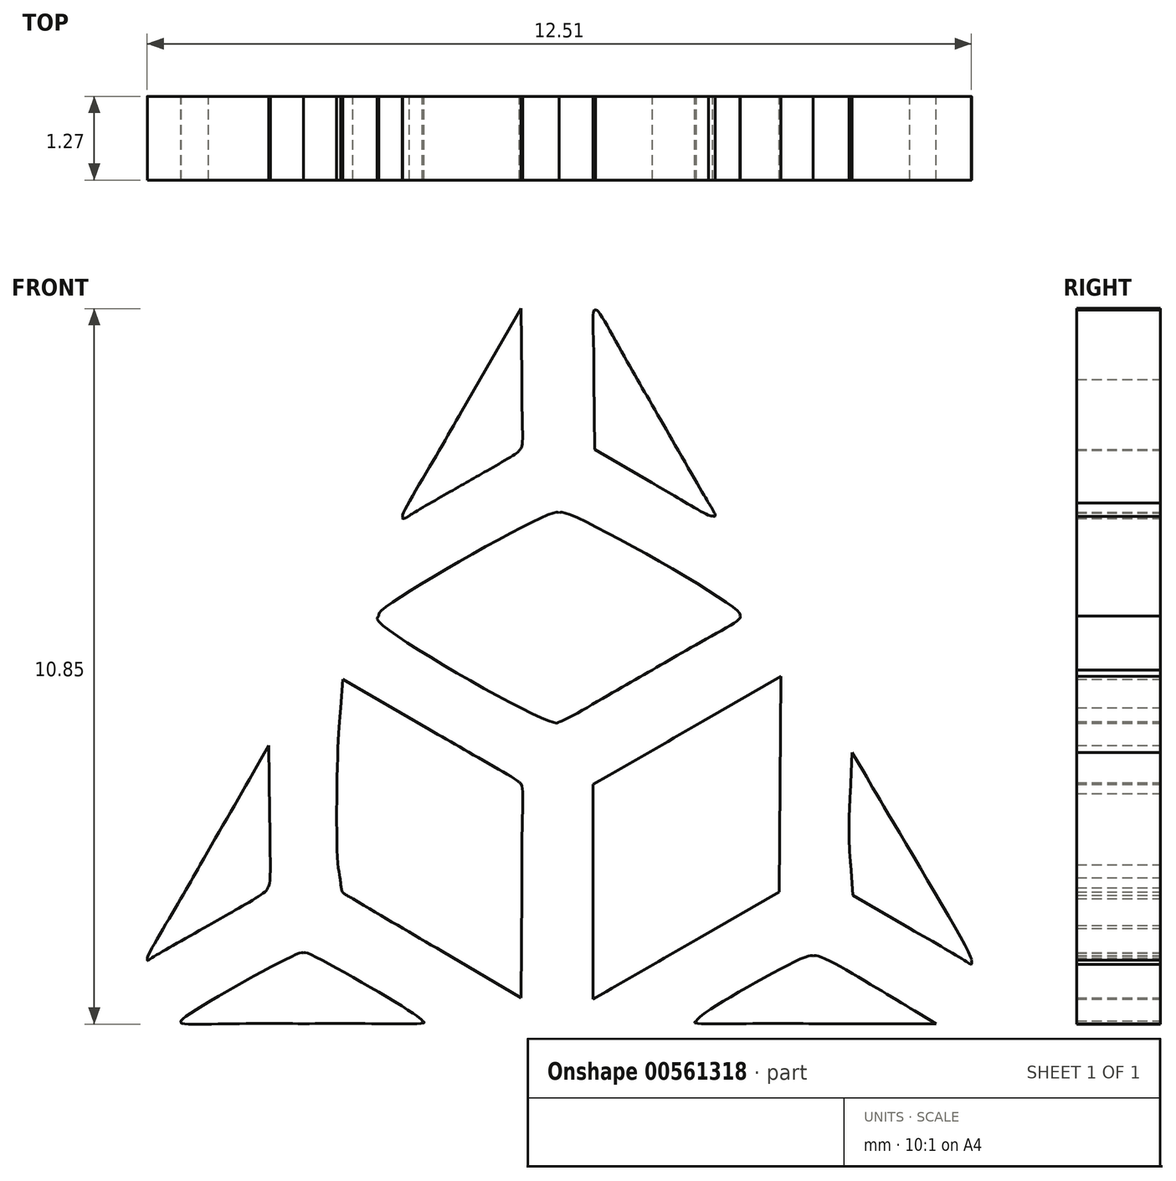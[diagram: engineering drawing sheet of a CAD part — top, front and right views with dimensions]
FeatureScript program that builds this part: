
annotation { "Feature Type Name" : "Feature", "Feature Type Description" : "" }
export const myFeature = defineFeature(function(context is Context, id is Id, definition is map)
    precondition{}
    {
        {
            var Q0;
            Q0=qCreatedBy(makeId("Front.planeOp"),FACE);
            var sketch = newSketch(context, id + "F0", { "sketchPlane" : qUnion([Q0])});
            skFitSpline(sketch, "E0", {"points": [v(-7.56, -9.6) * mm, v(-7.82, -9.54) * mm, v(-7.9, -9.44) * mm, v(-7.9, -9.18) * mm]});
            skFitSpline(sketch, "E1", {"points": [v(-7.9, -9.18) * mm, v(-7.89, -8.9) * mm, v(-8.03, -9.18) * mm, v(-5.89, -5.46) * mm]});
            skFitSpline(sketch, "E2", {"points": [v(-5.89, -5.46) * mm, v(-4.98, -3.9) * mm, v(-3.48, -1.3) * mm, v(-2.55, 0.32) * mm]});
            skFitSpline(sketch, "E3", {"points": [v(-2.55, 0.32) * mm, v(0.18, 5.07) * mm, v(0.04, 4.84) * mm, v(0.3, 4.9) * mm]});
            skFitSpline(sketch, "E4", {"points": [v(0.3, 4.9) * mm, v(0.37, 4.9) * mm, v(0.5, 4.9) * mm, v(0.57, 4.87) * mm]});
            skFitSpline(sketch, "E5", {"points": [v(0.57, 4.87) * mm, v(0.72, 4.82) * mm, v(0.6, 5.03) * mm, v(4.94, -2.5) * mm]});
            skFitSpline(sketch, "E6", {"points": [v(4.94, -2.5) * mm, v(8.66, -8.94) * mm, v(8.66, -8.95) * mm, v(8.68, -9.15) * mm]});
            skFitSpline(sketch, "E7", {"points": [v(8.68, -9.15) * mm, v(8.7, -9.4) * mm, v(8.64, -9.53) * mm, v(8.42, -9.59) * mm]});
            skFitSpline(sketch, "E8", {"points": [v(8.42, -9.59) * mm, v(8.22, -9.64) * mm, v(-7.27, -9.65) * mm, v(-7.56, -9.6) * mm]});
            skFitSpline(sketch, "E9", {"points": [v(-1.7, -8.52) * mm, v(-1.77, -8.45) * mm, v(-3.45, -7.5) * mm, v(-3.5, -7.5) * mm]});
            skFitSpline(sketch, "E10", {"points": [v(-3.5, -7.5) * mm, v(-3.55, -7.5) * mm, v(-5.35, -8.52) * mm, v(-5.35, -8.55) * mm]});
            skFitSpline(sketch, "E11", {"points": [v(-5.35, -8.55) * mm, v(-5.35, -8.56) * mm, v(-4.52, -8.56) * mm, v(-3.5, -8.56) * mm]});
            skFitSpline(sketch, "E12", {"points": [v(-3.5, -8.56) * mm, v(-2.41, -8.56) * mm, v(-1.67, -8.55) * mm, v(-1.7, -8.52) * mm]});
            skLineSegment(sketch, "E13", {"start": v(-7.56, -9.6) * mm, "end": v(-7.56, -9.6) * mm});
            skFitSpline(sketch, "E14", {"points": [v(5.85, -8.4) * mm, v(5.13, -7.98) * mm, v(4.32, -7.54) * mm, v(4.24, -7.54) * mm]});
            skFitSpline(sketch, "E15", {"points": [v(4.24, -7.54) * mm, v(4.16, -7.54) * mm, v(2.58, -8.42) * mm, v(2.47, -8.52) * mm]});
            skFitSpline(sketch, "E16", {"points": [v(2.47, -8.52) * mm, v(2.44, -8.55) * mm, v(3.17, -8.56) * mm, v(4.26, -8.56) * mm]});
            skFitSpline(sketch, "E17", {"points": [v(-0.22, -4.9) * mm, v(-0.24, -4.88) * mm, v(-0.86, -4.52) * mm, v(-1.58, -4.1) * mm]});
            skLineSegment(sketch, "E18", {"start": v(4.26, -8.56) * mm, "end": v(6.1, -8.56) * mm});
            skLineSegment(sketch, "E19", {"start": v(6.1, -8.56) * mm, "end": v(5.85, -8.4) * mm});
            skLineSegment(sketch, "E20", {"start": v(5.85, -8.4) * mm, "end": v(5.85, -8.4) * mm});
            skFitSpline(sketch, "E21", {"points": [v(-2.93, -3.77) * mm, v(-2.97, -4.36) * mm, v(-2.98, -6.07) * mm, v(-2.94, -6.35) * mm]});
            skFitSpline(sketch, "E22", {"points": [v(-2.94, -6.35) * mm, v(-2.92, -6.54) * mm, v(-2.89, -6.58) * mm, v(-2.75, -6.67) * mm]});
            skFitSpline(sketch, "E23", {"points": [v(-2.75, -6.67) * mm, v(-2.66, -6.72) * mm, v(-2.05, -7.08) * mm, v(-1.39, -7.47) * mm]});
            skLineSegment(sketch, "E24", {"start": v(-1.58, -4.1) * mm, "end": v(-2.9, -3.34) * mm});
            skLineSegment(sketch, "E25", {"start": v(-2.9, -3.34) * mm, "end": v(-2.93, -3.77) * mm});
            skFitSpline(sketch, "E26", {"points": [v(-0.18, -6.56) * mm, v(-0.18, -5.56) * mm, v(-0.19, -4.94) * mm, v(-0.22, -4.9) * mm]});
            skLineSegment(sketch, "E27", {"start": v(-1.39, -7.47) * mm, "end": v(-0.2, -8.17) * mm});
            skLineSegment(sketch, "E28", {"start": v(-0.2, -8.17) * mm, "end": v(-0.18, -6.56) * mm});
            skFitSpline(sketch, "E29", {"points": [v(2.57, -3.97) * mm, v(1.92, -4.35) * mm, v(1.28, -4.72) * mm, v(1.15, -4.8) * mm]});
            skLineSegment(sketch, "E30", {"start": v(2.51, -7.26) * mm, "end": v(3.72, -6.56) * mm});
            skLineSegment(sketch, "E31", {"start": v(3.72, -6.56) * mm, "end": v(3.74, -4.93) * mm});
            skLineSegment(sketch, "E32", {"start": v(3.74, -4.93) * mm, "end": v(3.75, -3.3) * mm});
            skLineSegment(sketch, "E33", {"start": v(3.75, -3.3) * mm, "end": v(2.57, -3.97) * mm});
            skFitSpline(sketch, "E34", {"points": [v(1.1, -8.08) * mm, v(1.2, -8.01) * mm, v(1.84, -7.65) * mm, v(2.51, -7.26) * mm]});
            skLineSegment(sketch, "E35", {"start": v(1.15, -4.8) * mm, "end": v(0.9, -4.93) * mm});
            skLineSegment(sketch, "E36", {"start": v(0.9, -4.93) * mm, "end": v(0.9, -6.56) * mm});
            skLineSegment(sketch, "E37", {"start": v(0.9, -6.56) * mm, "end": v(0.9, -8.2) * mm});
            skLineSegment(sketch, "E38", {"start": v(0.9, -8.2) * mm, "end": v(1.1, -8.08) * mm});
            skFitSpline(sketch, "E39", {"points": [v(6.64, -7.6) * mm, v(6.64, -7.58) * mm, v(5.53, -5.63) * mm, v(5, -4.75) * mm]});
            skFitSpline(sketch, "E40", {"points": [v(4.8, -5.07) * mm, v(4.79, -5.41) * mm, v(4.79, -5.9) * mm, v(4.8, -6.15) * mm]});
            skLineSegment(sketch, "E41", {"start": v(5, -4.75) * mm, "end": v(4.83, -4.45) * mm});
            skLineSegment(sketch, "E42", {"start": v(4.83, -4.45) * mm, "end": v(4.8, -5.07) * mm});
            skFitSpline(sketch, "E43", {"points": [v(5.7, -7.12) * mm, v(6.55, -7.62) * mm, v(6.64, -7.66) * mm, v(6.64, -7.6) * mm]});
            skLineSegment(sketch, "E44", {"start": v(4.8, -6.15) * mm, "end": v(4.84, -6.61) * mm});
            skLineSegment(sketch, "E45", {"start": v(4.84, -6.61) * mm, "end": v(5.7, -7.12) * mm});
            skFitSpline(sketch, "E46", {"points": [v(-4.94, -7.07) * mm, v(-4.47, -6.8) * mm, v(-4.07, -6.55) * mm, v(-4.04, -6.5) * mm]});
            skFitSpline(sketch, "E47", {"points": [v(-4.04, -6.5) * mm, v(-4.02, -6.46) * mm, v(-4, -5.97) * mm, v(-4, -5.38) * mm]});
            skFitSpline(sketch, "E48", {"points": [v(-4.14, -4.55) * mm, v(-4.2, -4.67) * mm, v(-4.62, -5.39) * mm, v(-5.06, -6.15) * mm]});
            skFitSpline(sketch, "E49", {"points": [v(-5.06, -6.15) * mm, v(-5.5, -6.92) * mm, v(-5.86, -7.55) * mm, v(-5.86, -7.57) * mm]});
            skFitSpline(sketch, "E50", {"points": [v(-5.86, -7.57) * mm, v(-5.86, -7.6) * mm, v(-5.84, -7.59) * mm, v(-4.94, -7.07) * mm]});
            skLineSegment(sketch, "E51", {"start": v(-4, -5.38) * mm, "end": v(-4.02, -4.34) * mm});
            skLineSegment(sketch, "E52", {"start": v(-4.02, -4.34) * mm, "end": v(-4.14, -4.55) * mm});
            skFitSpline(sketch, "E53", {"points": [v(1.8, -3.2) * mm, v(2.54, -2.77) * mm, v(3.13, -2.4) * mm, v(3.12, -2.38) * mm]});
            skFitSpline(sketch, "E54", {"points": [v(3.12, -2.38) * mm, v(3.1, -2.31) * mm, v(0.48, -0.82) * mm, v(0.38, -0.82) * mm]});
            skFitSpline(sketch, "E55", {"points": [v(0.38, -0.82) * mm, v(0.29, -0.82) * mm, v(-2.33, -2.32) * mm, v(-2.35, -2.38) * mm]});
            skFitSpline(sketch, "E56", {"points": [v(-2.35, -2.38) * mm, v(-2.37, -2.44) * mm, v(0.3, -4) * mm, v(0.39, -3.98) * mm]});
            skFitSpline(sketch, "E57", {"points": [v(0.39, -3.98) * mm, v(0.43, -3.97) * mm, v(1.06, -3.62) * mm, v(1.8, -3.2) * mm]});
            skFitSpline(sketch, "E58", {"points": [v(-1.03, -0.36) * mm, v(-0.61, -0.12) * mm, v(-0.25, 0.1) * mm, v(-0.22, 0.14) * mm]});
            skFitSpline(sketch, "E59", {"points": [v(-0.22, 0.14) * mm, v(-0.19, 0.18) * mm, v(-0.18, 0.55) * mm, v(-0.18, 1.24) * mm]});
            skFitSpline(sketch, "E60", {"points": [v(-1.1, 0.73) * mm, v(-1.59, -0.13) * mm, v(-2, -0.85) * mm, v(-2, -0.88) * mm]});
            skFitSpline(sketch, "E61", {"points": [v(-2, -0.88) * mm, v(-2, -0.9) * mm, v(-1.95, -0.9) * mm, v(-1.89, -0.86) * mm]});
            skFitSpline(sketch, "E62", {"points": [v(-1.89, -0.86) * mm, v(-1.83, -0.82) * mm, v(-1.44, -0.6) * mm, v(-1.03, -0.36) * mm]});
            skLineSegment(sketch, "E63", {"start": v(-0.18, 1.24) * mm, "end": v(-0.2, 2.28) * mm});
            skLineSegment(sketch, "E64", {"start": v(-0.2, 2.28) * mm, "end": v(-1.1, 0.73) * mm});
            skFitSpline(sketch, "E65", {"points": [v(2.65, -0.67) * mm, v(2.59, -0.56) * mm, v(2.18, 0.14) * mm, v(1.75, 0.9) * mm]});
            skFitSpline(sketch, "E66", {"points": [v(1.75, 0.9) * mm, v(1.32, 1.65) * mm, v(0.95, 2.26) * mm, v(0.93, 2.26) * mm]});
            skFitSpline(sketch, "E67", {"points": [v(0.93, 2.26) * mm, v(0.91, 2.26) * mm, v(0.9, 1.79) * mm, v(0.91, 1.2) * mm]});
            skFitSpline(sketch, "E68", {"points": [v(1.79, -0.36) * mm, v(2.26, -0.63) * mm, v(2.68, -0.86) * mm, v(2.71, -0.86) * mm]});
            skFitSpline(sketch, "E69", {"points": [v(2.71, -0.86) * mm, v(2.75, -0.86) * mm, v(2.73, -0.8) * mm, v(2.65, -0.67) * mm]});
            skLineSegment(sketch, "E70", {"start": v(0.91, 1.2) * mm, "end": v(0.92, 0.15) * mm});
            skLineSegment(sketch, "E71", {"start": v(0.92, 0.15) * mm, "end": v(1.79, -0.36) * mm});
            skSolve(sketch);
        }
        {
            var Q0;
            Q0 = qSketchRegion(id + "F0", true);
            extrude(context, id + "F1", {"entities" : qUnion([Q0]), "depth" : 1.27 * mm, "offsetDistance" : 25.4 * mm});
        }
    });
